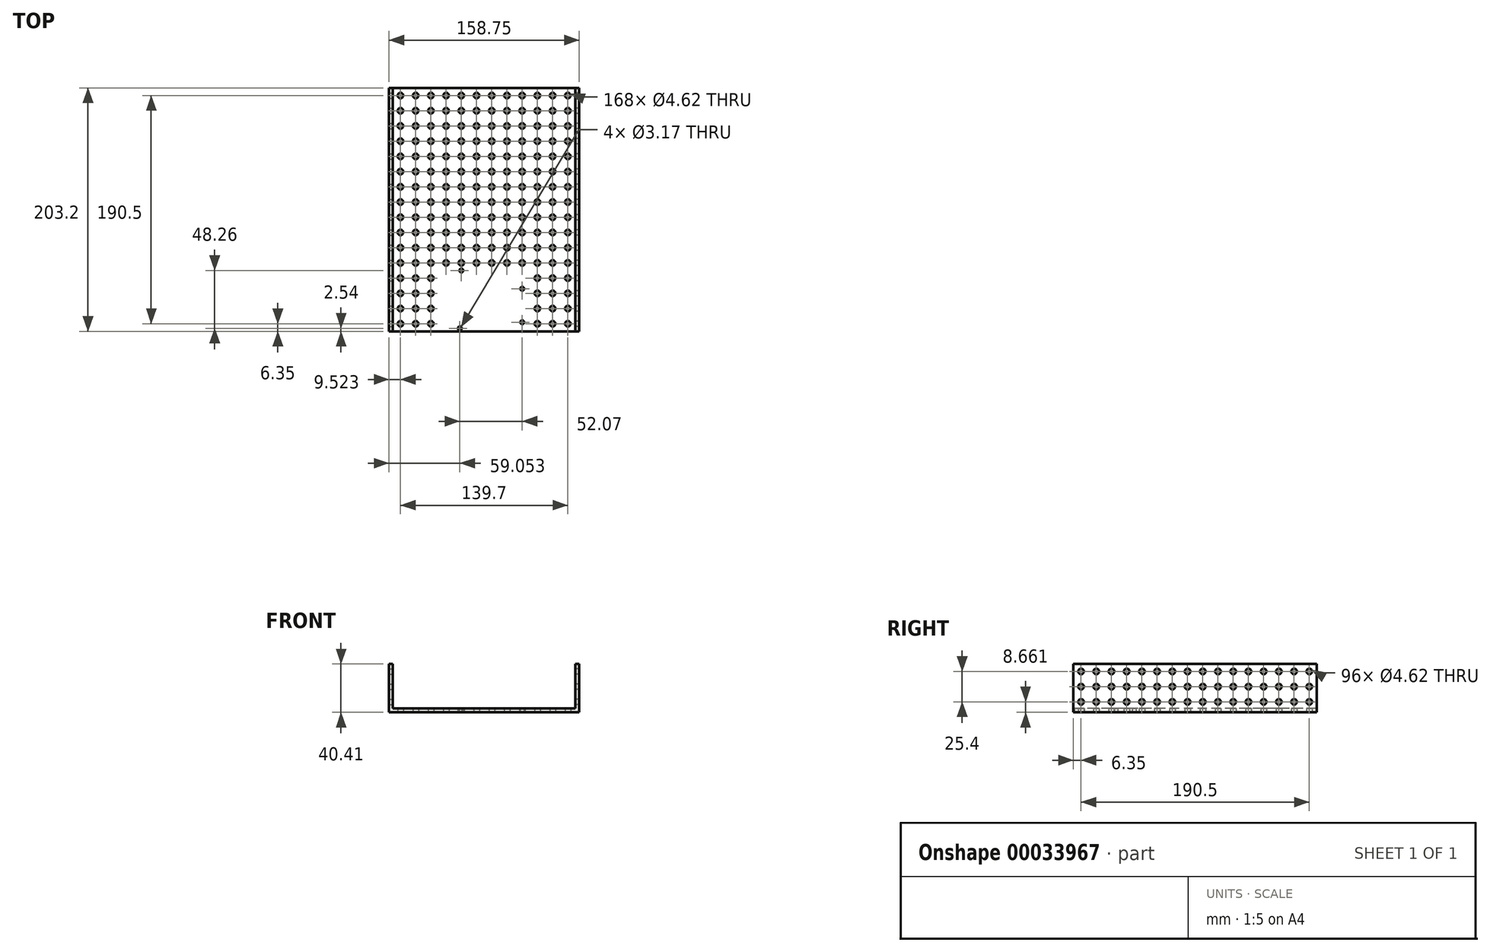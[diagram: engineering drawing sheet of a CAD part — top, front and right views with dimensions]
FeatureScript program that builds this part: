
annotation { "Feature Type Name" : "Feature", "Feature Type Description" : "" }
export const myFeature = defineFeature(function(context is Context, id is Id, definition is map)
    precondition{}
    {
        {
            var Q0;
            Q0=qCreatedBy(makeId("Top.planeOp"),FACE);
            var sketch = newSketch(context, id + "F0", { "sketchPlane" : qUnion([Q0])});
            skLineSegment(sketch, "E0.bottom", {"start": v(-81.24, 121.15) * mm, "end": v(71.16, 121.15) * mm});
            skLineSegment(sketch, "E0.top", {"start": v(-81.24, -82.05) * mm, "end": v(71.16, -82.05) * mm});
            skLineSegment(sketch, "E0.left", {"start": v(-81.24, 121.15) * mm, "end": v(-81.24, -82.05) * mm});
            skLineSegment(sketch, "E0.right", {"start": v(71.16, 121.15) * mm, "end": v(71.16, -82.05) * mm});
            skPoint(sketch, "E1", {"position": v(-81.24, 117.11) * mm});
            skCircle(sketch, "E2", {"center": v(-74.89, 114.8) * mm, "radius": 2.31 * mm});
            skCircle(sketch, "E3.0.1.0", {"center": v(-74.89, 102.1) * mm, "radius": 2.31 * mm});
            skCircle(sketch, "E3.0.2.0", {"center": v(-74.89, 89.4) * mm, "radius": 2.31 * mm});
            skCircle(sketch, "E3.0.3.0", {"center": v(-74.89, 76.7) * mm, "radius": 2.31 * mm});
            skCircle(sketch, "E3.0.4.0", {"center": v(-74.89, 64) * mm, "radius": 2.31 * mm});
            skCircle(sketch, "E3.0.5.0", {"center": v(-74.89, 51.3) * mm, "radius": 2.31 * mm});
            skCircle(sketch, "E3.0.6.0", {"center": v(-74.89, 38.6) * mm, "radius": 2.31 * mm});
            skCircle(sketch, "E3.0.7.0", {"center": v(-74.89, 25.9) * mm, "radius": 2.31 * mm});
            skCircle(sketch, "E3.0.8.0", {"center": v(-74.89, 13.2) * mm, "radius": 2.31 * mm});
            skCircle(sketch, "E3.0.9.0", {"center": v(-74.89, 0.5) * mm, "radius": 2.31 * mm});
            skCircle(sketch, "E3.0.10.0", {"center": v(-74.89, -12.2) * mm, "radius": 2.31 * mm});
            skCircle(sketch, "E3.0.11.0", {"center": v(-74.89, -24.9) * mm, "radius": 2.31 * mm});
            skCircle(sketch, "E3.0.12.0", {"center": v(-74.89, -37.6) * mm, "radius": 2.31 * mm});
            skCircle(sketch, "E3.0.13.0", {"center": v(-74.89, -50.3) * mm, "radius": 2.31 * mm});
            skCircle(sketch, "E3.0.14.0", {"center": v(-74.89, -63) * mm, "radius": 2.31 * mm});
            skCircle(sketch, "E3.1.0.0", {"center": v(-62.19, 114.8) * mm, "radius": 2.31 * mm});
            skCircle(sketch, "E3.1.1.0", {"center": v(-62.19, 102.1) * mm, "radius": 2.31 * mm});
            skCircle(sketch, "E3.1.2.0", {"center": v(-62.19, 89.4) * mm, "radius": 2.31 * mm});
            skCircle(sketch, "E3.1.3.0", {"center": v(-62.19, 76.7) * mm, "radius": 2.31 * mm});
            skCircle(sketch, "E3.1.4.0", {"center": v(-62.19, 64) * mm, "radius": 2.31 * mm});
            skCircle(sketch, "E3.1.5.0", {"center": v(-62.19, 51.3) * mm, "radius": 2.31 * mm});
            skCircle(sketch, "E3.1.6.0", {"center": v(-62.19, 38.6) * mm, "radius": 2.31 * mm});
            skCircle(sketch, "E3.1.7.0", {"center": v(-62.19, 25.9) * mm, "radius": 2.31 * mm});
            skCircle(sketch, "E3.1.8.0", {"center": v(-62.19, 13.2) * mm, "radius": 2.31 * mm});
            skCircle(sketch, "E3.1.9.0", {"center": v(-62.19, 0.5) * mm, "radius": 2.31 * mm});
            skCircle(sketch, "E3.1.10.0", {"center": v(-62.19, -12.2) * mm, "radius": 2.31 * mm});
            skCircle(sketch, "E3.1.11.0", {"center": v(-62.19, -24.9) * mm, "radius": 2.31 * mm});
            skCircle(sketch, "E3.1.12.0", {"center": v(-62.19, -37.6) * mm, "radius": 2.31 * mm});
            skCircle(sketch, "E3.1.13.0", {"center": v(-62.19, -50.3) * mm, "radius": 2.31 * mm});
            skCircle(sketch, "E3.1.14.0", {"center": v(-62.19, -63) * mm, "radius": 2.31 * mm});
            skCircle(sketch, "E3.2.0.0", {"center": v(-49.49, 114.8) * mm, "radius": 2.31 * mm});
            skCircle(sketch, "E3.2.1.0", {"center": v(-49.49, 102.1) * mm, "radius": 2.31 * mm});
            skCircle(sketch, "E3.2.2.0", {"center": v(-49.49, 89.4) * mm, "radius": 2.31 * mm});
            skCircle(sketch, "E3.2.3.0", {"center": v(-49.49, 76.7) * mm, "radius": 2.31 * mm});
            skCircle(sketch, "E3.2.4.0", {"center": v(-49.49, 64) * mm, "radius": 2.31 * mm});
            skCircle(sketch, "E3.2.5.0", {"center": v(-49.49, 51.3) * mm, "radius": 2.31 * mm});
            skCircle(sketch, "E3.2.6.0", {"center": v(-49.49, 38.6) * mm, "radius": 2.31 * mm});
            skCircle(sketch, "E3.2.7.0", {"center": v(-49.49, 25.9) * mm, "radius": 2.31 * mm});
            skCircle(sketch, "E3.2.8.0", {"center": v(-49.49, 13.2) * mm, "radius": 2.31 * mm});
            skCircle(sketch, "E3.2.9.0", {"center": v(-49.49, 0.5) * mm, "radius": 2.31 * mm});
            skCircle(sketch, "E3.2.10.0", {"center": v(-49.49, -12.2) * mm, "radius": 2.31 * mm});
            skCircle(sketch, "E3.2.11.0", {"center": v(-49.49, -24.9) * mm, "radius": 2.31 * mm});
            skCircle(sketch, "E3.2.12.0", {"center": v(-49.49, -37.6) * mm, "radius": 2.31 * mm});
            skCircle(sketch, "E3.2.13.0", {"center": v(-49.49, -50.3) * mm, "radius": 2.31 * mm});
            skCircle(sketch, "E3.2.14.0", {"center": v(-49.49, -63) * mm, "radius": 2.31 * mm});
            skCircle(sketch, "E3.3.0.0", {"center": v(-36.79, 114.8) * mm, "radius": 2.31 * mm});
            skCircle(sketch, "E3.3.1.0", {"center": v(-36.79, 102.1) * mm, "radius": 2.31 * mm});
            skCircle(sketch, "E3.3.2.0", {"center": v(-36.79, 89.4) * mm, "radius": 2.31 * mm});
            skCircle(sketch, "E3.3.3.0", {"center": v(-36.79, 76.7) * mm, "radius": 2.31 * mm});
            skCircle(sketch, "E3.3.4.0", {"center": v(-36.79, 64) * mm, "radius": 2.31 * mm});
            skCircle(sketch, "E3.3.5.0", {"center": v(-36.79, 51.3) * mm, "radius": 2.31 * mm});
            skCircle(sketch, "E3.3.6.0", {"center": v(-36.79, 38.6) * mm, "radius": 2.31 * mm});
            skCircle(sketch, "E3.3.7.0", {"center": v(-36.79, 25.9) * mm, "radius": 2.31 * mm});
            skCircle(sketch, "E3.3.8.0", {"center": v(-36.79, 13.2) * mm, "radius": 2.31 * mm});
            skCircle(sketch, "E3.3.9.0", {"center": v(-36.79, 0.5) * mm, "radius": 2.31 * mm});
            skCircle(sketch, "E3.3.10.0", {"center": v(-36.79, -12.2) * mm, "radius": 2.31 * mm});
            skCircle(sketch, "E3.3.11.0", {"center": v(-36.79, -24.9) * mm, "radius": 2.31 * mm});
            skCircle(sketch, "E3.4.0.0", {"center": v(-24.09, 114.8) * mm, "radius": 2.31 * mm});
            skCircle(sketch, "E3.4.1.0", {"center": v(-24.09, 102.1) * mm, "radius": 2.31 * mm});
            skCircle(sketch, "E3.4.2.0", {"center": v(-24.09, 89.4) * mm, "radius": 2.31 * mm});
            skCircle(sketch, "E3.4.3.0", {"center": v(-24.09, 76.7) * mm, "radius": 2.31 * mm});
            skCircle(sketch, "E3.4.4.0", {"center": v(-24.09, 64) * mm, "radius": 2.31 * mm});
            skCircle(sketch, "E3.4.5.0", {"center": v(-24.09, 51.3) * mm, "radius": 2.31 * mm});
            skCircle(sketch, "E3.4.6.0", {"center": v(-24.09, 38.6) * mm, "radius": 2.31 * mm});
            skCircle(sketch, "E3.4.7.0", {"center": v(-24.09, 25.9) * mm, "radius": 2.31 * mm});
            skCircle(sketch, "E3.4.8.0", {"center": v(-24.09, 13.2) * mm, "radius": 2.31 * mm});
            skCircle(sketch, "E3.4.9.0", {"center": v(-24.09, 0.5) * mm, "radius": 2.31 * mm});
            skCircle(sketch, "E3.4.10.0", {"center": v(-24.09, -12.2) * mm, "radius": 2.31 * mm});
            skCircle(sketch, "E3.4.11.0", {"center": v(-24.09, -24.9) * mm, "radius": 2.31 * mm});
            skCircle(sketch, "E3.5.0.0", {"center": v(-11.39, 114.8) * mm, "radius": 2.31 * mm});
            skCircle(sketch, "E3.5.1.0", {"center": v(-11.39, 102.1) * mm, "radius": 2.31 * mm});
            skCircle(sketch, "E3.5.2.0", {"center": v(-11.39, 89.4) * mm, "radius": 2.31 * mm});
            skCircle(sketch, "E3.5.3.0", {"center": v(-11.39, 76.7) * mm, "radius": 2.31 * mm});
            skCircle(sketch, "E3.5.4.0", {"center": v(-11.39, 64) * mm, "radius": 2.31 * mm});
            skCircle(sketch, "E3.5.5.0", {"center": v(-11.39, 51.3) * mm, "radius": 2.31 * mm});
            skCircle(sketch, "E3.5.6.0", {"center": v(-11.39, 38.6) * mm, "radius": 2.31 * mm});
            skCircle(sketch, "E3.5.7.0", {"center": v(-11.39, 25.9) * mm, "radius": 2.31 * mm});
            skCircle(sketch, "E3.5.8.0", {"center": v(-11.39, 13.2) * mm, "radius": 2.31 * mm});
            skCircle(sketch, "E3.5.9.0", {"center": v(-11.39, 0.5) * mm, "radius": 2.31 * mm});
            skCircle(sketch, "E3.5.10.0", {"center": v(-11.39, -12.2) * mm, "radius": 2.31 * mm});
            skCircle(sketch, "E3.5.11.0", {"center": v(-11.39, -24.9) * mm, "radius": 2.31 * mm});
            skCircle(sketch, "E3.6.0.0", {"center": v(1.31, 114.8) * mm, "radius": 2.31 * mm});
            skCircle(sketch, "E3.6.1.0", {"center": v(1.31, 102.1) * mm, "radius": 2.31 * mm});
            skCircle(sketch, "E3.6.2.0", {"center": v(1.31, 89.4) * mm, "radius": 2.31 * mm});
            skCircle(sketch, "E3.6.3.0", {"center": v(1.31, 76.7) * mm, "radius": 2.31 * mm});
            skCircle(sketch, "E3.6.4.0", {"center": v(1.31, 64) * mm, "radius": 2.31 * mm});
            skCircle(sketch, "E3.6.5.0", {"center": v(1.31, 51.3) * mm, "radius": 2.31 * mm});
            skCircle(sketch, "E3.6.6.0", {"center": v(1.31, 38.6) * mm, "radius": 2.31 * mm});
            skCircle(sketch, "E3.6.7.0", {"center": v(1.31, 25.9) * mm, "radius": 2.31 * mm});
            skCircle(sketch, "E3.6.8.0", {"center": v(1.31, 13.2) * mm, "radius": 2.31 * mm});
            skCircle(sketch, "E3.6.9.0", {"center": v(1.31, 0.5) * mm, "radius": 2.31 * mm});
            skCircle(sketch, "E3.6.10.0", {"center": v(1.31, -12.2) * mm, "radius": 2.31 * mm});
            skCircle(sketch, "E3.6.11.0", {"center": v(1.31, -24.9) * mm, "radius": 2.31 * mm});
            skCircle(sketch, "E3.7.0.0", {"center": v(14.01, 114.8) * mm, "radius": 2.31 * mm});
            skCircle(sketch, "E3.7.1.0", {"center": v(14.01, 102.1) * mm, "radius": 2.31 * mm});
            skCircle(sketch, "E3.7.2.0", {"center": v(14.01, 89.4) * mm, "radius": 2.31 * mm});
            skCircle(sketch, "E3.7.3.0", {"center": v(14.01, 76.7) * mm, "radius": 2.31 * mm});
            skCircle(sketch, "E3.7.4.0", {"center": v(14.01, 64) * mm, "radius": 2.31 * mm});
            skCircle(sketch, "E3.7.5.0", {"center": v(14.01, 51.3) * mm, "radius": 2.31 * mm});
            skCircle(sketch, "E3.7.6.0", {"center": v(14.01, 38.6) * mm, "radius": 2.31 * mm});
            skCircle(sketch, "E3.7.7.0", {"center": v(14.01, 25.9) * mm, "radius": 2.31 * mm});
            skCircle(sketch, "E3.7.8.0", {"center": v(14.01, 13.2) * mm, "radius": 2.31 * mm});
            skCircle(sketch, "E3.7.9.0", {"center": v(14.01, 0.5) * mm, "radius": 2.31 * mm});
            skCircle(sketch, "E3.7.10.0", {"center": v(14.01, -12.2) * mm, "radius": 2.31 * mm});
            skCircle(sketch, "E3.7.11.0", {"center": v(14.01, -24.9) * mm, "radius": 2.31 * mm});
            skCircle(sketch, "E3.8.0.0", {"center": v(26.71, 114.8) * mm, "radius": 2.31 * mm});
            skCircle(sketch, "E3.8.1.0", {"center": v(26.71, 102.1) * mm, "radius": 2.31 * mm});
            skCircle(sketch, "E3.8.2.0", {"center": v(26.71, 89.4) * mm, "radius": 2.31 * mm});
            skCircle(sketch, "E3.8.3.0", {"center": v(26.71, 76.7) * mm, "radius": 2.31 * mm});
            skCircle(sketch, "E3.8.4.0", {"center": v(26.71, 64) * mm, "radius": 2.31 * mm});
            skCircle(sketch, "E3.8.5.0", {"center": v(26.71, 51.3) * mm, "radius": 2.31 * mm});
            skCircle(sketch, "E3.8.6.0", {"center": v(26.71, 38.6) * mm, "radius": 2.31 * mm});
            skCircle(sketch, "E3.8.7.0", {"center": v(26.71, 25.9) * mm, "radius": 2.31 * mm});
            skCircle(sketch, "E3.8.8.0", {"center": v(26.71, 13.2) * mm, "radius": 2.31 * mm});
            skCircle(sketch, "E3.8.9.0", {"center": v(26.71, 0.5) * mm, "radius": 2.31 * mm});
            skCircle(sketch, "E3.8.10.0", {"center": v(26.71, -12.2) * mm, "radius": 2.31 * mm});
            skCircle(sketch, "E3.8.11.0", {"center": v(26.71, -24.9) * mm, "radius": 2.31 * mm});
            skCircle(sketch, "E3.9.0.0", {"center": v(39.41, 114.8) * mm, "radius": 2.31 * mm});
            skCircle(sketch, "E3.9.1.0", {"center": v(39.41, 102.1) * mm, "radius": 2.31 * mm});
            skCircle(sketch, "E3.9.2.0", {"center": v(39.41, 89.4) * mm, "radius": 2.31 * mm});
            skCircle(sketch, "E3.9.3.0", {"center": v(39.41, 76.7) * mm, "radius": 2.31 * mm});
            skCircle(sketch, "E3.9.4.0", {"center": v(39.41, 64) * mm, "radius": 2.31 * mm});
            skCircle(sketch, "E3.9.5.0", {"center": v(39.41, 51.3) * mm, "radius": 2.31 * mm});
            skCircle(sketch, "E3.9.6.0", {"center": v(39.41, 38.6) * mm, "radius": 2.31 * mm});
            skCircle(sketch, "E3.9.7.0", {"center": v(39.41, 25.9) * mm, "radius": 2.31 * mm});
            skCircle(sketch, "E3.9.8.0", {"center": v(39.41, 13.2) * mm, "radius": 2.31 * mm});
            skCircle(sketch, "E3.9.9.0", {"center": v(39.41, 0.5) * mm, "radius": 2.31 * mm});
            skCircle(sketch, "E3.9.10.0", {"center": v(39.41, -12.2) * mm, "radius": 2.31 * mm});
            skCircle(sketch, "E3.9.11.0", {"center": v(39.41, -24.9) * mm, "radius": 2.31 * mm});
            skCircle(sketch, "E3.9.12.0", {"center": v(39.41, -37.6) * mm, "radius": 2.31 * mm});
            skCircle(sketch, "E3.9.13.0", {"center": v(39.41, -50.3) * mm, "radius": 2.31 * mm});
            skCircle(sketch, "E3.9.14.0", {"center": v(39.41, -63) * mm, "radius": 2.31 * mm});
            skCircle(sketch, "E3.10.0.0", {"center": v(52.11, 114.8) * mm, "radius": 2.31 * mm});
            skCircle(sketch, "E3.10.1.0", {"center": v(52.11, 102.1) * mm, "radius": 2.31 * mm});
            skCircle(sketch, "E3.10.2.0", {"center": v(52.11, 89.4) * mm, "radius": 2.31 * mm});
            skCircle(sketch, "E3.10.3.0", {"center": v(52.11, 76.7) * mm, "radius": 2.31 * mm});
            skCircle(sketch, "E3.10.4.0", {"center": v(52.11, 64) * mm, "radius": 2.31 * mm});
            skCircle(sketch, "E3.10.5.0", {"center": v(52.11, 51.3) * mm, "radius": 2.31 * mm});
            skCircle(sketch, "E3.10.6.0", {"center": v(52.11, 38.6) * mm, "radius": 2.31 * mm});
            skCircle(sketch, "E3.10.7.0", {"center": v(52.11, 25.9) * mm, "radius": 2.31 * mm});
            skCircle(sketch, "E3.10.8.0", {"center": v(52.11, 13.2) * mm, "radius": 2.31 * mm});
            skCircle(sketch, "E3.10.9.0", {"center": v(52.11, 0.5) * mm, "radius": 2.31 * mm});
            skCircle(sketch, "E3.10.10.0", {"center": v(52.11, -12.2) * mm, "radius": 2.31 * mm});
            skCircle(sketch, "E3.10.11.0", {"center": v(52.11, -24.9) * mm, "radius": 2.31 * mm});
            skCircle(sketch, "E3.10.12.0", {"center": v(52.11, -37.6) * mm, "radius": 2.31 * mm});
            skCircle(sketch, "E3.10.13.0", {"center": v(52.11, -50.3) * mm, "radius": 2.31 * mm});
            skCircle(sketch, "E3.10.14.0", {"center": v(52.11, -63) * mm, "radius": 2.31 * mm});
            skLineSegment(sketch, "E3.direction1", {"start": v(-74.89, 114.8) * mm, "end": v(-62.19, 114.8) * mm, "construction": true});
            skLineSegment(sketch, "E3.direction2", {"start": v(-74.89, 114.8) * mm, "end": v(-74.89, 102.1) * mm, "construction": true});
            skCircle(sketch, "E4.0.11.0", {"center": v(64.81, 114.8) * mm, "radius": 2.31 * mm});
            skCircle(sketch, "E4.0.11.1", {"center": v(64.81, 102.1) * mm, "radius": 2.31 * mm});
            skCircle(sketch, "E4.0.11.2", {"center": v(64.81, 89.4) * mm, "radius": 2.31 * mm});
            skCircle(sketch, "E4.0.11.3", {"center": v(64.81, 76.7) * mm, "radius": 2.31 * mm});
            skCircle(sketch, "E4.0.11.4", {"center": v(64.81, 64) * mm, "radius": 2.31 * mm});
            skCircle(sketch, "E4.0.11.5", {"center": v(64.81, 51.3) * mm, "radius": 2.31 * mm});
            skCircle(sketch, "E4.0.11.6", {"center": v(64.81, 38.6) * mm, "radius": 2.31 * mm});
            skCircle(sketch, "E4.0.11.7", {"center": v(64.81, 25.9) * mm, "radius": 2.31 * mm});
            skCircle(sketch, "E4.0.11.8", {"center": v(64.81, 13.2) * mm, "radius": 2.31 * mm});
            skCircle(sketch, "E4.0.11.9", {"center": v(64.81, 0.5) * mm, "radius": 2.31 * mm});
            skCircle(sketch, "E4.0.11.10", {"center": v(64.81, -12.2) * mm, "radius": 2.31 * mm});
            skCircle(sketch, "E4.0.11.11", {"center": v(64.81, -24.9) * mm, "radius": 2.31 * mm});
            skCircle(sketch, "E4.0.11.12", {"center": v(64.81, -37.6) * mm, "radius": 2.31 * mm});
            skCircle(sketch, "E4.0.11.13", {"center": v(64.81, -50.3) * mm, "radius": 2.31 * mm});
            skCircle(sketch, "E4.0.11.14", {"center": v(64.81, -63) * mm, "radius": 2.31 * mm});
            skCircle(sketch, "E5.0.0.15", {"center": v(-74.89, -75.7) * mm, "radius": 2.31 * mm});
            skCircle(sketch, "E5.0.1.15", {"center": v(-62.19, -75.7) * mm, "radius": 2.31 * mm});
            skCircle(sketch, "E5.0.2.15", {"center": v(-49.49, -75.7) * mm, "radius": 2.31 * mm});
            skCircle(sketch, "E5.0.9.15", {"center": v(39.41, -75.7) * mm, "radius": 2.31 * mm});
            skCircle(sketch, "E5.0.10.15", {"center": v(52.11, -75.7) * mm, "radius": 2.31 * mm});
            skCircle(sketch, "E5.0.11.15", {"center": v(64.81, -75.7) * mm, "radius": 2.31 * mm});
            skLineSegment(sketch, "E6.bottom", {"start": v(29.25, -82.05) * mm, "end": v(-39.33, -82.05) * mm});
            skLineSegment(sketch, "E6.top", {"start": v(29.25, -28.7) * mm, "end": v(-39.33, -28.7) * mm});
            skLineSegment(sketch, "E6.left", {"start": v(29.25, -82.05) * mm, "end": v(29.25, -28.7) * mm});
            skLineSegment(sketch, "E6.right", {"start": v(-39.33, -82.05) * mm, "end": v(-39.33, -28.7) * mm});
            skPoint(sketch, "E7", {"position": v(-39.33, -79.5) * mm});
            skLineSegment(sketch, "E8", {"start": v(-39.33, -79.5) * mm, "end": v(-25.36, -79.5) * mm});
            skCircle(sketch, "E9", {"center": v(-25.36, -79.5) * mm, "radius": 1.59 * mm});
            skPoint(sketch, "E10", {"position": v(-39.33, -31.25) * mm});
            skLineSegment(sketch, "E11", {"start": v(-39.33, -31.25) * mm, "end": v(-24.09, -31.25) * mm});
            skCircle(sketch, "E12", {"center": v(-24.09, -31.25) * mm, "radius": 1.59 * mm});
            skPoint(sketch, "E13", {"position": v(26.71, -28.7) * mm});
            skLineSegment(sketch, "E14", {"start": v(26.71, -28.7) * mm, "end": v(26.71, -46.49) * mm});
            skCircle(sketch, "E15", {"center": v(26.71, -46.49) * mm, "radius": 1.59 * mm});
            skLineSegment(sketch, "E16", {"start": v(26.71, -28.7) * mm, "end": v(26.71, -74.43) * mm});
            skCircle(sketch, "E17", {"center": v(26.71, -74.43) * mm, "radius": 1.59 * mm});
            skSolve(sketch);
        }
        {
            var Q0;
            Q0 = qSketchRegion(id + "F0", true);
            extrude(context, id + "F1", {"entities" : qUnion([Q0]), "depth" : 3.17 * mm});
        }
        {
            var Q0;
            Q0=makeQuery(id+"F1.opExtrude","SWEPT_FACE",FACE,{"disambiguationData":[OSD([sQuery(id+"F0.wireOp",EDGE,"E0.left")])]});
            var sketch = newSketch(context, id + "F2", { "sketchPlane" : qUnion([Q0])});
            skLineSegment(sketch, "E18.bottom", {"start": v(-121.15, 0) * mm, "end": v(82.05, 0) * mm});
            skLineSegment(sketch, "E18.top", {"start": v(-121.15, 40.41) * mm, "end": v(82.05, 40.41) * mm});
            skLineSegment(sketch, "E18.left", {"start": v(-121.15, 0) * mm, "end": v(-121.15, 40.41) * mm});
            skLineSegment(sketch, "E18.right", {"start": v(82.05, 0) * mm, "end": v(82.05, 40.41) * mm});
            skPoint(sketch, "E19", {"position": v(-117.11, 0) * mm});
            skLineSegment(sketch, "E20.bottom", {"start": v(-121.15, 40.41) * mm, "end": v(-117.11, 40.41) * mm});
            skLineSegment(sketch, "E20.left", {"start": v(-121.15, 40.41) * mm, "end": v(-121.15, 36.37) * mm});
            skCircle(sketch, "E21", {"center": v(-114.8, 34.06) * mm, "radius": 2.31 * mm});
            skPoint(sketch, "E22.orphan", {"position": v(-112.49, 36.37) * mm});
            skPoint(sketch, "E23.right.end.orphan", {"position": v(-112.49, 31.75) * mm});
            skPoint(sketch, "E23.right.start.orphan", {"position": v(-112.49, 34.06) * mm});
            skCircle(sketch, "E24.0.1.0", {"center": v(-114.8, 21.36) * mm, "radius": 2.31 * mm});
            skCircle(sketch, "E24.0.2.0", {"center": v(-114.8, 8.66) * mm, "radius": 2.31 * mm});
            skCircle(sketch, "E24.1.0.0", {"center": v(-102.1, 34.06) * mm, "radius": 2.31 * mm});
            skCircle(sketch, "E24.1.1.0", {"center": v(-102.1, 21.36) * mm, "radius": 2.31 * mm});
            skCircle(sketch, "E24.1.2.0", {"center": v(-102.1, 8.66) * mm, "radius": 2.31 * mm});
            skCircle(sketch, "E24.2.0.0", {"center": v(-89.4, 34.06) * mm, "radius": 2.31 * mm});
            skCircle(sketch, "E24.2.1.0", {"center": v(-89.4, 21.36) * mm, "radius": 2.31 * mm});
            skCircle(sketch, "E24.2.2.0", {"center": v(-89.4, 8.66) * mm, "radius": 2.31 * mm});
            skCircle(sketch, "E24.3.0.0", {"center": v(-76.7, 34.06) * mm, "radius": 2.31 * mm});
            skCircle(sketch, "E24.3.1.0", {"center": v(-76.7, 21.36) * mm, "radius": 2.31 * mm});
            skCircle(sketch, "E24.3.2.0", {"center": v(-76.7, 8.66) * mm, "radius": 2.31 * mm});
            skCircle(sketch, "E24.4.0.0", {"center": v(-64, 34.06) * mm, "radius": 2.31 * mm});
            skCircle(sketch, "E24.4.1.0", {"center": v(-64, 21.36) * mm, "radius": 2.31 * mm});
            skCircle(sketch, "E24.4.2.0", {"center": v(-64, 8.66) * mm, "radius": 2.31 * mm});
            skCircle(sketch, "E24.5.0.0", {"center": v(-51.3, 34.06) * mm, "radius": 2.31 * mm});
            skCircle(sketch, "E24.5.1.0", {"center": v(-51.3, 21.36) * mm, "radius": 2.31 * mm});
            skCircle(sketch, "E24.5.2.0", {"center": v(-51.3, 8.66) * mm, "radius": 2.31 * mm});
            skCircle(sketch, "E24.6.0.0", {"center": v(-38.6, 34.06) * mm, "radius": 2.31 * mm});
            skCircle(sketch, "E24.6.1.0", {"center": v(-38.6, 21.36) * mm, "radius": 2.31 * mm});
            skCircle(sketch, "E24.6.2.0", {"center": v(-38.6, 8.66) * mm, "radius": 2.31 * mm});
            skCircle(sketch, "E24.7.0.0", {"center": v(-25.9, 34.06) * mm, "radius": 2.31 * mm});
            skCircle(sketch, "E24.7.1.0", {"center": v(-25.9, 21.36) * mm, "radius": 2.31 * mm});
            skCircle(sketch, "E24.7.2.0", {"center": v(-25.9, 8.66) * mm, "radius": 2.31 * mm});
            skCircle(sketch, "E24.8.0.0", {"center": v(-13.2, 34.06) * mm, "radius": 2.31 * mm});
            skCircle(sketch, "E24.8.1.0", {"center": v(-13.2, 21.36) * mm, "radius": 2.31 * mm});
            skCircle(sketch, "E24.8.2.0", {"center": v(-13.2, 8.66) * mm, "radius": 2.31 * mm});
            skCircle(sketch, "E24.9.0.0", {"center": v(-0.5, 34.06) * mm, "radius": 2.31 * mm});
            skCircle(sketch, "E24.9.1.0", {"center": v(-0.5, 21.36) * mm, "radius": 2.31 * mm});
            skCircle(sketch, "E24.9.2.0", {"center": v(-0.5, 8.66) * mm, "radius": 2.31 * mm});
            skCircle(sketch, "E24.10.0.0", {"center": v(12.2, 34.06) * mm, "radius": 2.31 * mm});
            skCircle(sketch, "E24.10.1.0", {"center": v(12.2, 21.36) * mm, "radius": 2.31 * mm});
            skCircle(sketch, "E24.10.2.0", {"center": v(12.2, 8.66) * mm, "radius": 2.31 * mm});
            skCircle(sketch, "E24.11.0.0", {"center": v(24.9, 34.06) * mm, "radius": 2.31 * mm});
            skCircle(sketch, "E24.11.1.0", {"center": v(24.9, 21.36) * mm, "radius": 2.31 * mm});
            skCircle(sketch, "E24.11.2.0", {"center": v(24.9, 8.66) * mm, "radius": 2.31 * mm});
            skCircle(sketch, "E24.12.0.0", {"center": v(37.6, 34.06) * mm, "radius": 2.31 * mm});
            skCircle(sketch, "E24.12.1.0", {"center": v(37.6, 21.36) * mm, "radius": 2.31 * mm});
            skCircle(sketch, "E24.12.2.0", {"center": v(37.6, 8.66) * mm, "radius": 2.31 * mm});
            skCircle(sketch, "E24.13.0.0", {"center": v(50.3, 34.06) * mm, "radius": 2.31 * mm});
            skCircle(sketch, "E24.13.1.0", {"center": v(50.3, 21.36) * mm, "radius": 2.31 * mm});
            skCircle(sketch, "E24.13.2.0", {"center": v(50.3, 8.66) * mm, "radius": 2.31 * mm});
            skCircle(sketch, "E24.14.0.0", {"center": v(63, 34.06) * mm, "radius": 2.31 * mm});
            skCircle(sketch, "E24.14.1.0", {"center": v(63, 21.36) * mm, "radius": 2.31 * mm});
            skCircle(sketch, "E24.14.2.0", {"center": v(63, 8.66) * mm, "radius": 2.31 * mm});
            skCircle(sketch, "E24.15.0.0", {"center": v(75.7, 34.06) * mm, "radius": 2.31 * mm});
            skCircle(sketch, "E24.15.1.0", {"center": v(75.7, 21.36) * mm, "radius": 2.31 * mm});
            skCircle(sketch, "E24.15.2.0", {"center": v(75.7, 8.66) * mm, "radius": 2.31 * mm});
            skLineSegment(sketch, "E24.direction1", {"start": v(-114.8, 34.06) * mm, "end": v(-102.1, 34.06) * mm, "construction": true});
            skLineSegment(sketch, "E24.direction2", {"start": v(-114.8, 34.06) * mm, "end": v(-114.8, 21.36) * mm, "construction": true});
            skSolve(sketch);
        }
        {
            var Q0;
            Q0 = qSketchRegion(id + "F2", true);
            var Q1;
            {var subQ2=sQuery(id+"F2.wireOp",EDGE,"E18.bottom");Q1=makeQuery(id+"F2.imprint","IMPRINT",FACE,{"disambiguationData":[TD([[makeQuery(id+"F2.imprint","IMPRINT",EDGE,{"derivedFrom":subQ2}),1.0]])]});}
            extrude(context, id + "F3", {"entities" : qUnion([Q0, Q1]), "operationType" : NewBodyOperationType.ADD, "depth" : 3.17 * mm});
        }
        {
            var Q0;
            Q0=makeQuery(id+"F1.opExtrude","SWEPT_FACE",FACE,{"disambiguationData":[OSD([sQuery(id+"F0.wireOp",EDGE,"E0.right")])]});
            var sketch = newSketch(context, id + "F4", { "sketchPlane" : qUnion([Q0])});
            skLineSegment(sketch, "E25.bottom", {"start": v(-82.05, 0) * mm, "end": v(121.15, 0) * mm});
            skLineSegment(sketch, "E25.top", {"start": v(-82.05, 40.41) * mm, "end": v(121.15, 40.41) * mm});
            skLineSegment(sketch, "E25.left", {"start": v(-82.05, 0) * mm, "end": v(-82.05, 40.41) * mm});
            skLineSegment(sketch, "E25.right", {"start": v(121.15, 0) * mm, "end": v(121.15, 40.41) * mm});
            skPoint(sketch, "E26", {"position": v(-78.01, 0) * mm});
            skLineSegment(sketch, "E27.bottom", {"start": v(-82.05, 40.41) * mm, "end": v(-78.01, 40.41) * mm});
            skLineSegment(sketch, "E27.left", {"start": v(-82.05, 40.41) * mm, "end": v(-82.05, 36.37) * mm});
            skCircle(sketch, "E28", {"center": v(-75.7, 34.06) * mm, "radius": 2.31 * mm});
            skPoint(sketch, "E29.orphan", {"position": v(-73.39, 31.75) * mm});
            skPoint(sketch, "E30.orphan", {"position": v(-73.39, 36.37) * mm});
            skPoint(sketch, "E31.start.orphan", {"position": v(-73.39, 34.06) * mm});
            skCircle(sketch, "E32.0.1.0", {"center": v(-75.7, 21.36) * mm, "radius": 2.31 * mm});
            skCircle(sketch, "E32.0.2.0", {"center": v(-75.7, 8.66) * mm, "radius": 2.31 * mm});
            skCircle(sketch, "E32.1.0.0", {"center": v(-63, 34.06) * mm, "radius": 2.31 * mm});
            skCircle(sketch, "E32.1.1.0", {"center": v(-63, 21.36) * mm, "radius": 2.31 * mm});
            skCircle(sketch, "E32.1.2.0", {"center": v(-63, 8.66) * mm, "radius": 2.31 * mm});
            skCircle(sketch, "E32.2.0.0", {"center": v(-50.3, 34.06) * mm, "radius": 2.31 * mm});
            skCircle(sketch, "E32.2.1.0", {"center": v(-50.3, 21.36) * mm, "radius": 2.31 * mm});
            skCircle(sketch, "E32.2.2.0", {"center": v(-50.3, 8.66) * mm, "radius": 2.31 * mm});
            skCircle(sketch, "E32.3.0.0", {"center": v(-37.6, 34.06) * mm, "radius": 2.31 * mm});
            skCircle(sketch, "E32.3.1.0", {"center": v(-37.6, 21.36) * mm, "radius": 2.31 * mm});
            skCircle(sketch, "E32.3.2.0", {"center": v(-37.6, 8.66) * mm, "radius": 2.31 * mm});
            skCircle(sketch, "E32.4.0.0", {"center": v(-24.9, 34.06) * mm, "radius": 2.31 * mm});
            skCircle(sketch, "E32.4.1.0", {"center": v(-24.9, 21.36) * mm, "radius": 2.31 * mm});
            skCircle(sketch, "E32.4.2.0", {"center": v(-24.9, 8.66) * mm, "radius": 2.31 * mm});
            skCircle(sketch, "E32.5.0.0", {"center": v(-12.2, 34.06) * mm, "radius": 2.31 * mm});
            skCircle(sketch, "E32.5.1.0", {"center": v(-12.2, 21.36) * mm, "radius": 2.31 * mm});
            skCircle(sketch, "E32.5.2.0", {"center": v(-12.2, 8.66) * mm, "radius": 2.31 * mm});
            skCircle(sketch, "E32.6.0.0", {"center": v(0.5, 34.06) * mm, "radius": 2.31 * mm});
            skCircle(sketch, "E32.6.1.0", {"center": v(0.5, 21.36) * mm, "radius": 2.31 * mm});
            skCircle(sketch, "E32.6.2.0", {"center": v(0.5, 8.66) * mm, "radius": 2.31 * mm});
            skCircle(sketch, "E32.7.0.0", {"center": v(13.2, 34.06) * mm, "radius": 2.31 * mm});
            skCircle(sketch, "E32.7.1.0", {"center": v(13.2, 21.36) * mm, "radius": 2.31 * mm});
            skCircle(sketch, "E32.7.2.0", {"center": v(13.2, 8.66) * mm, "radius": 2.31 * mm});
            skCircle(sketch, "E32.8.0.0", {"center": v(25.9, 34.06) * mm, "radius": 2.31 * mm});
            skCircle(sketch, "E32.8.1.0", {"center": v(25.9, 21.36) * mm, "radius": 2.31 * mm});
            skCircle(sketch, "E32.8.2.0", {"center": v(25.9, 8.66) * mm, "radius": 2.31 * mm});
            skCircle(sketch, "E32.9.0.0", {"center": v(38.6, 34.06) * mm, "radius": 2.31 * mm});
            skCircle(sketch, "E32.9.1.0", {"center": v(38.6, 21.36) * mm, "radius": 2.31 * mm});
            skCircle(sketch, "E32.9.2.0", {"center": v(38.6, 8.66) * mm, "radius": 2.31 * mm});
            skCircle(sketch, "E32.10.0.0", {"center": v(51.3, 34.06) * mm, "radius": 2.31 * mm});
            skCircle(sketch, "E32.10.1.0", {"center": v(51.3, 21.36) * mm, "radius": 2.31 * mm});
            skCircle(sketch, "E32.10.2.0", {"center": v(51.3, 8.66) * mm, "radius": 2.31 * mm});
            skCircle(sketch, "E32.11.0.0", {"center": v(64, 34.06) * mm, "radius": 2.31 * mm});
            skCircle(sketch, "E32.11.1.0", {"center": v(64, 21.36) * mm, "radius": 2.31 * mm});
            skCircle(sketch, "E32.11.2.0", {"center": v(64, 8.66) * mm, "radius": 2.31 * mm});
            skCircle(sketch, "E32.12.0.0", {"center": v(76.7, 34.06) * mm, "radius": 2.31 * mm});
            skCircle(sketch, "E32.12.1.0", {"center": v(76.7, 21.36) * mm, "radius": 2.31 * mm});
            skCircle(sketch, "E32.12.2.0", {"center": v(76.7, 8.66) * mm, "radius": 2.31 * mm});
            skCircle(sketch, "E32.13.0.0", {"center": v(89.4, 34.06) * mm, "radius": 2.31 * mm});
            skCircle(sketch, "E32.13.1.0", {"center": v(89.4, 21.36) * mm, "radius": 2.31 * mm});
            skCircle(sketch, "E32.13.2.0", {"center": v(89.4, 8.66) * mm, "radius": 2.31 * mm});
            skCircle(sketch, "E32.14.0.0", {"center": v(102.1, 34.06) * mm, "radius": 2.31 * mm});
            skCircle(sketch, "E32.14.1.0", {"center": v(102.1, 21.36) * mm, "radius": 2.31 * mm});
            skCircle(sketch, "E32.14.2.0", {"center": v(102.1, 8.66) * mm, "radius": 2.31 * mm});
            skCircle(sketch, "E32.15.0.0", {"center": v(114.8, 34.06) * mm, "radius": 2.31 * mm});
            skCircle(sketch, "E32.15.1.0", {"center": v(114.8, 21.36) * mm, "radius": 2.31 * mm});
            skCircle(sketch, "E32.15.2.0", {"center": v(114.8, 8.66) * mm, "radius": 2.31 * mm});
            skLineSegment(sketch, "E32.direction1", {"start": v(-75.7, 34.06) * mm, "end": v(-63, 34.06) * mm, "construction": true});
            skLineSegment(sketch, "E32.direction2", {"start": v(-75.7, 34.06) * mm, "end": v(-75.7, 21.36) * mm, "construction": true});
            skSolve(sketch);
        }
        {
            var Q0;
            {var subQ2=sQuery(id+"F4.wireOp",EDGE,"E25.bottom");Q0=makeQuery(id+"F4.imprint","IMPRINT",FACE,{"disambiguationData":[TD([[makeQuery(id+"F4.imprint","IMPRINT",EDGE,{"derivedFrom":subQ2}),-1.0]])]});}
            var Q1;
            {var subQ1=sQuery(id+"F4.wireOp",EDGE,"E25.top");Q1=makeQuery(id+"F4.imprint","IMPRINT",FACE,{"disambiguationData":[TD([[makeQuery(id+"F4.imprint","IMPRINT",EDGE,{"derivedFrom":subQ1}),-1.0]])]});}
            extrude(context, id + "F5", {"entities" : qUnion([Q0, Q1]), "operationType" : NewBodyOperationType.ADD, "depth" : 3.17 * mm});
        }
    });
